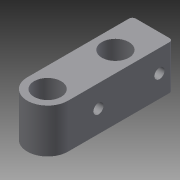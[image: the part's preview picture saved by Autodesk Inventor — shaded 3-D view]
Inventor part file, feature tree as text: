
AUTODESK INVENTOR PART (.ipt)
format: ipt  version: 2013 (Build 170138000, 138)  size: 118,784 bytes
history: native  units: mm
features: extrude x3, sketch x3, fillet x1
ambient origin geometry x8: Origin, YZ Plane, XZ Plane, XY Plane, X Axis, Y Axis, Z Axis, Center Point
bodies: Solid1 (feature_tree)
feature tree (7):
  extrude  "Extrusion1"  Depth=25.0mm
  extrude  "Extrusion2"  Depth=13.0mm TaperAngle=0.0deg
  extrude  "Extrusion3"  Depth=3.0mm
  fillet  "Fillet1"  Radius=18.0mm
  sketch  "Sketch1"  dims[d0=12.0mm d1=25.0mm]
  sketch  "Sketch2"  dims[d3=8.0mm d4=13.0mm d5=0.0mm]
  sketch  "Sketch3"  dims[d6=3.0mm d7=3.0mm d8=18.0mm d9=9.0mm d10=4.0mm d11=0.0mm d12=6.0mm d13=6.0mm d14=3.0mm d15=0.0mm d16=8.0mm d17=20.0mm d18=1.0mm]
